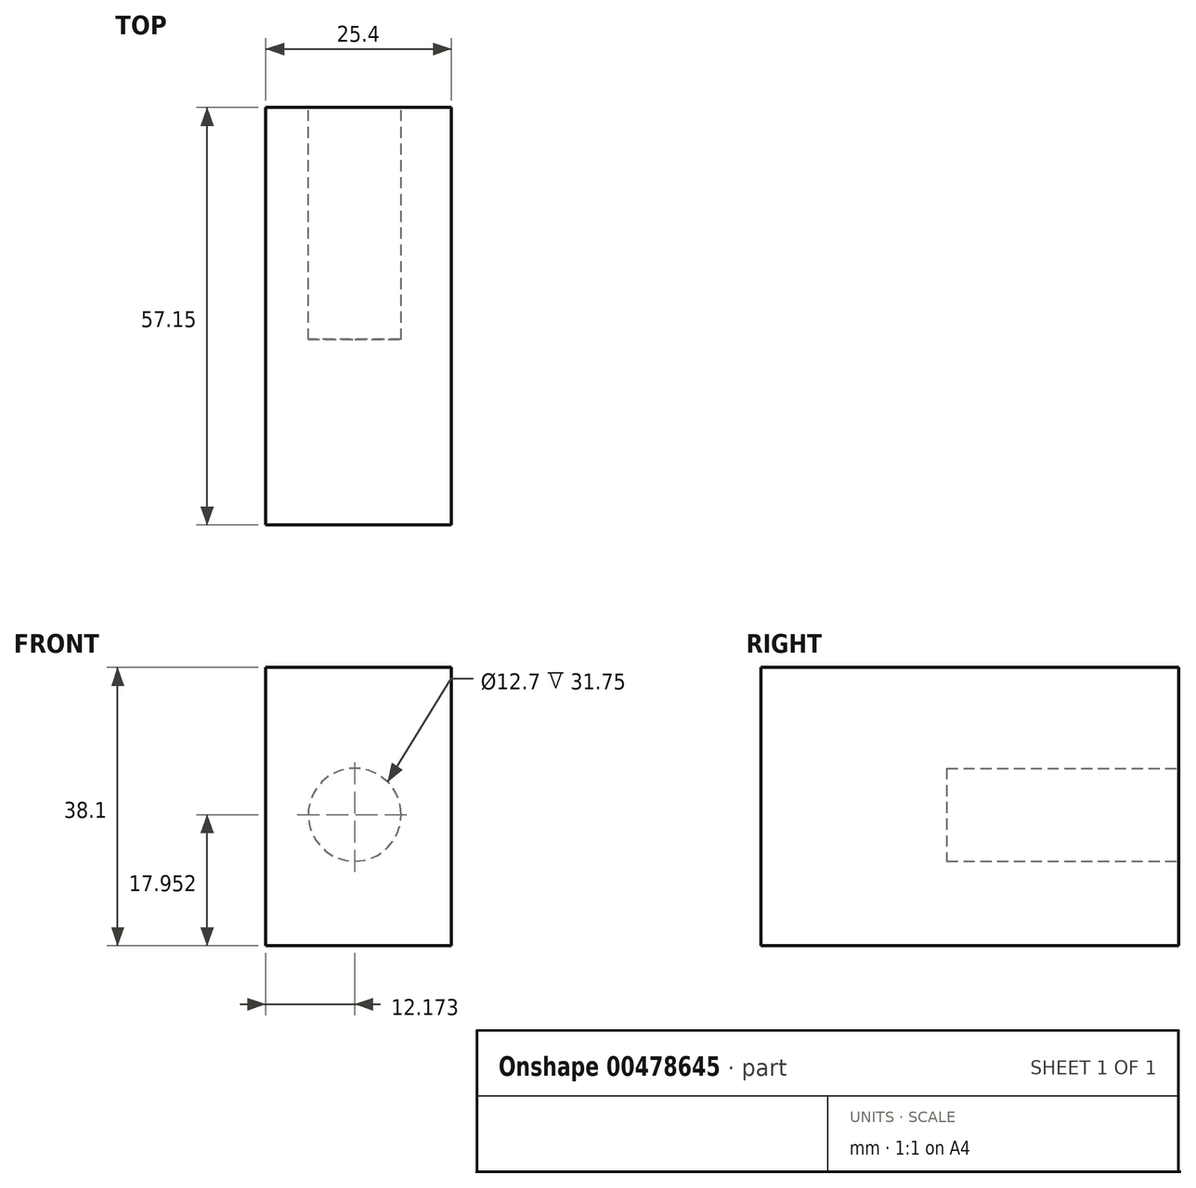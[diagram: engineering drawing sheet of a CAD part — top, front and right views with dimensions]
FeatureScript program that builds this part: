
annotation { "Feature Type Name" : "Feature", "Feature Type Description" : "" }
export const myFeature = defineFeature(function(context is Context, id is Id, definition is map)
    precondition{}
    {
        {
            var Q0;
            Q0=qCreatedBy(makeId("Front.planeOp"),FACE);
            var sketch = newSketch(context, id + "F0", { "sketchPlane" : qUnion([Q0])});
            skLineSegment(sketch, "E0.bottom", {"start": v(6.41, 41.02) * mm, "end": v(31.81, 41.02) * mm});
            skLineSegment(sketch, "E0.top", {"start": v(6.41, 2.92) * mm, "end": v(31.81, 2.92) * mm});
            skLineSegment(sketch, "E0.left", {"start": v(6.41, 41.02) * mm, "end": v(6.41, 2.92) * mm});
            skLineSegment(sketch, "E0.right", {"start": v(31.81, 41.02) * mm, "end": v(31.81, 2.92) * mm});
            skSolve(sketch);
        }
        {
            var Q0;
            Q0=makeQuery(id+"F0.imprint","IMPRINT",FACE,{"disambiguationData":[TD([[makeQuery(id+"F0.imprint","IMPRINT",EDGE,{"derivedFrom":sQuery(id+"F0.wireOp",EDGE,"E0.bottom")}),-1.0]])]});
            extrude(context, id + "F1", {"entities" : qUnion([Q0]), "depth" : 57.15 * mm});
        }
        {
            var Q0;
            Q0=makeQuery(id+"F1.opExtrude","CAP_FACE",FACE,{"disambiguationData":[OSD([sQuery(id+"F0.wireOp",EDGE,"E0.bottom"),sQuery(id+"F0.wireOp",EDGE,"E0.top"),sQuery(id+"F0.wireOp",EDGE,"E0.left"),sQuery(id+"F0.wireOp",EDGE,"E0.right")])],"isStart":true});
            var sketch = newSketch(context, id + "F2", { "sketchPlane" : qUnion([Q0])});
            skCircle(sketch, "E1", {"center": v(-18.58, 20.87) * mm, "radius": 6.35 * mm});
            skSolve(sketch);
        }
        {
            var Q0;
            Q0=makeQuery(id+"F2.imprint","IMPRINT",FACE,{"disambiguationData":[TD([[makeQuery(id+"F2.imprint","IMPRINT",EDGE,{"derivedFrom":sQuery(id+"F2.wireOp",EDGE,"E1")}),1.0]])]});
            extrude(context, id + "F3", {"entities" : qUnion([Q0]), "operationType" : NewBodyOperationType.REMOVE, "oppositeDirection" : true, "depth" : 31.75 * mm});
        }
    });
